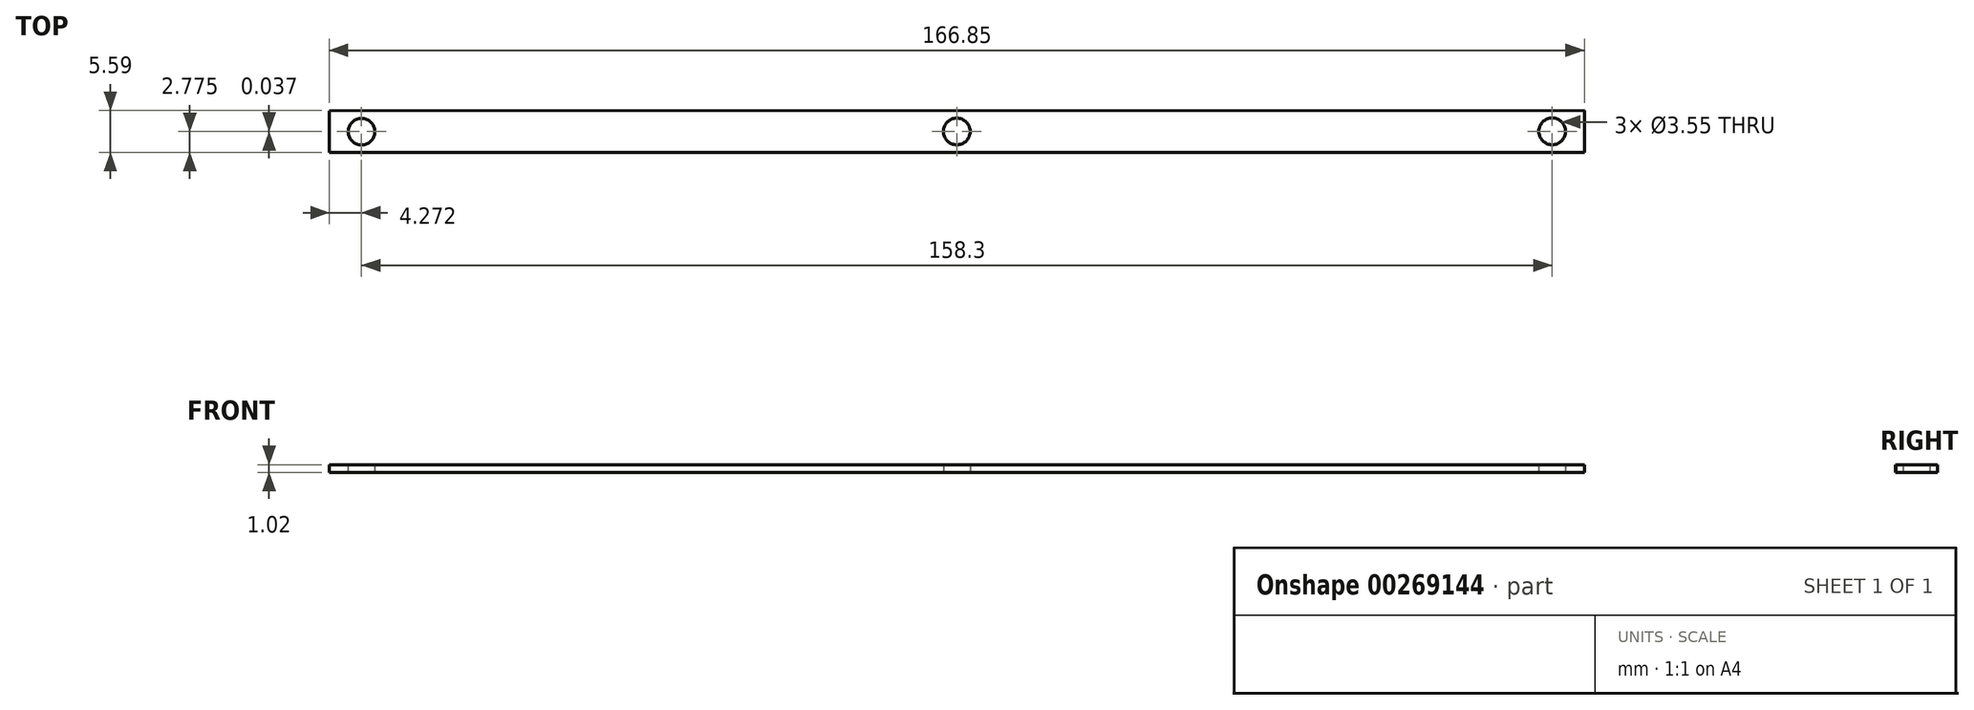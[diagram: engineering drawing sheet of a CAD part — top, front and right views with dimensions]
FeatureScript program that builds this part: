
annotation { "Feature Type Name" : "Feature", "Feature Type Description" : "" }
export const myFeature = defineFeature(function(context is Context, id is Id, definition is map)
    precondition{}
    {
        {
            var Q0;
            Q0=qCreatedBy(makeId("Top.planeOp"),FACE);
            var sketch = newSketch(context, id + "F0", { "sketchPlane" : qUnion([Q0])});
            skLineSegment(sketch, "E0.left", {"start": v(-81.7, 23.57) * mm, "end": v(-81.7, 18.02) * mm});
            skCircle(sketch, "E1", {"center": v(-77.43, 20.8) * mm, "radius": 1.77 * mm});
            skCircle(sketch, "E2", {"center": v(1.72, 20.81) * mm, "radius": 1.77 * mm});
            skCircle(sketch, "E3", {"center": v(80.87, 20.83) * mm, "radius": 1.77 * mm});
            skLineSegment(sketch, "E4", {"start": v(85.15, 23.6) * mm, "end": v(85.15, 18.06) * mm});
            skLineSegment(sketch, "E5", {"start": v(-81.7, 23.57) * mm, "end": v(85.15, 23.6) * mm});
            skLineSegment(sketch, "E6", {"start": v(-81.7, 18.02) * mm, "end": v(85.15, 18.06) * mm});
            skSolve(sketch);
        }
        {
            var Q0;
            Q0=makeQuery(id+"F0.imprint","IMPRINT",FACE,{"disambiguationData":[TD([[makeQuery(id+"F0.imprint","IMPRINT",EDGE,{"derivedFrom":sQuery(id+"F0.wireOp",EDGE,"E0.left")}),1.0]])]});
            extrude(context, id + "F1", {"entities" : qUnion([Q0]), "depth" : 1.02 * mm});
        }
    });
